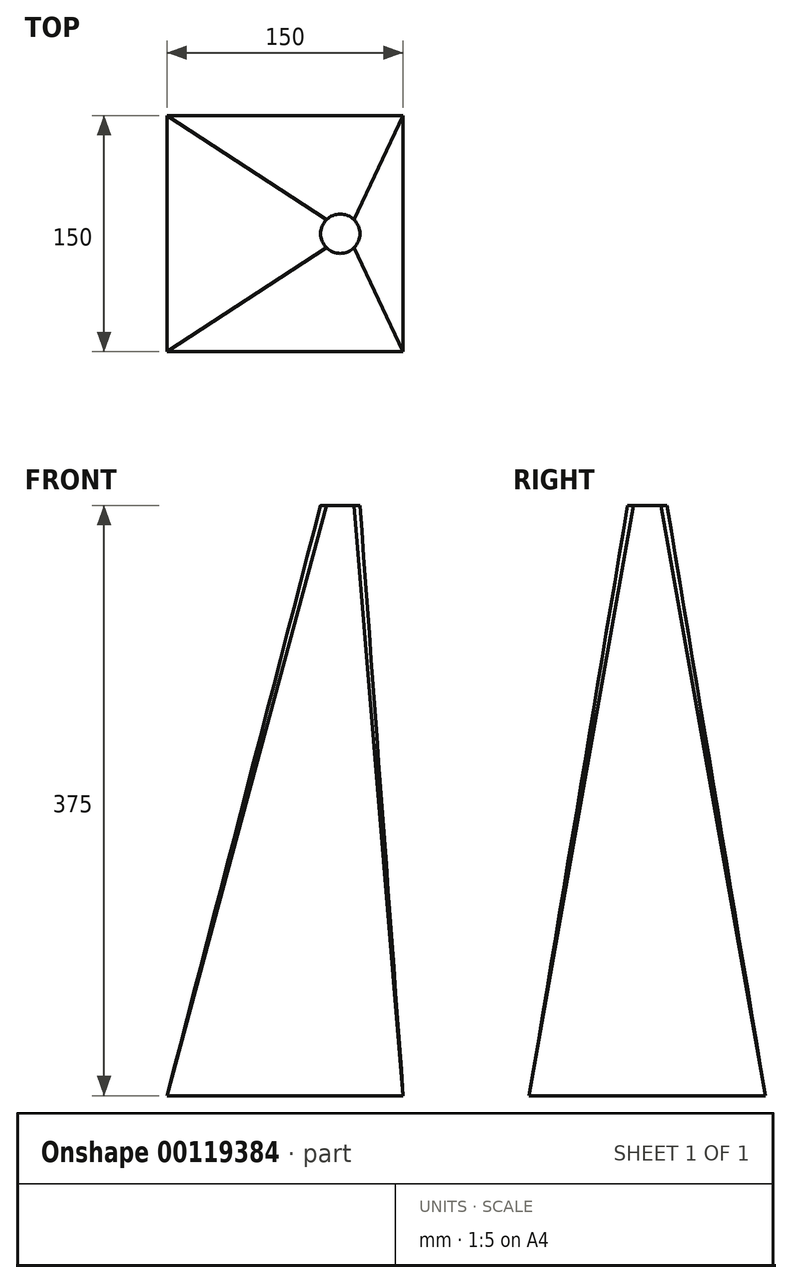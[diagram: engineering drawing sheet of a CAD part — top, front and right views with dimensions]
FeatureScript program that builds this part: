
annotation { "Feature Type Name" : "Feature", "Feature Type Description" : "" }
export const myFeature = defineFeature(function(context is Context, id is Id, definition is map)
    precondition{}
    {
        {
            var Q0;
            Q0=qCreatedBy(makeId("Top.planeOp"),FACE);
            var sketch = newSketch(context, id + "F0", { "sketchPlane" : qUnion([Q0])});
            skLineSegment(sketch, "E0.bottom", {"start": v(75, -75) * mm, "end": v(-75, -75) * mm});
            skLineSegment(sketch, "E0.top", {"start": v(75, 75) * mm, "end": v(-75, 75) * mm});
            skLineSegment(sketch, "E0.left", {"start": v(75, -75) * mm, "end": v(75, 75) * mm});
            skLineSegment(sketch, "E0.right", {"start": v(-75, -75) * mm, "end": v(-75, 75) * mm});
            skPoint(sketch, "E0.middle", {"position": v(0, 0) * mm});
            skSolve(sketch);
        }
        {
            var Q0;
            Q0=makeQuery(id+"F0.imprint","IMPRINT",FACE,{"disambiguationData":[TD([[makeQuery(id+"F0.imprint","IMPRINT",EDGE,{"derivedFrom":sQuery(id+"F0.wireOp",EDGE,"E0.bottom")}),-1.0]])]});
            cPlane(context, id + "F1", {"entities" : qUnion([Q0]), "cplaneType" : CPlaneType.OFFSET, "offset" : 375 * mm, "width" : 150 * mm, "height" : 150 * mm});
        }
        {
            var Q0;
            Q0=qCreatedBy(id+"F1.planeOp",FACE);
            var sketch = newSketch(context, id + "F2", { "sketchPlane" : qUnion([Q0])});
            skPoint(sketch, "E1.middle", {"position": v(35, 0) * mm});
            skLineSegment(sketch, "E2", {"start": v(35, 0) * mm, "end": v(26.16, -8.84) * mm, "construction": true});
            skLineSegment(sketch, "E3", {"start": v(35, 0) * mm, "end": v(26.16, 8.84) * mm, "construction": true});
            skLineSegment(sketch, "E4", {"start": v(35, 0) * mm, "end": v(43.84, 8.84) * mm, "construction": true});
            skLineSegment(sketch, "E5", {"start": v(35, 0) * mm, "end": v(43.84, -8.84) * mm, "construction": true});
            skArc(sketch, "E6", {"start": v(26.16, -8.84) * mm, "mid": v(35, -12.5) * mm, "end": v(43.84, -8.84) * mm});
            skArc(sketch, "E7", {"start": v(43.84, -8.84) * mm, "mid": v(47.5, 0) * mm, "end": v(43.84, 8.84) * mm});
            skLineSegment(sketch, "E8", {"start": v(43.84, 8.84) * mm, "end": v(43.84, 8.84) * mm});
            skArc(sketch, "E9", {"start": v(26.16, 8.84) * mm, "mid": v(22.5, 0) * mm, "end": v(26.16, -8.84) * mm});
            skArc(sketch, "E10", {"start": v(43.84, 8.84) * mm, "mid": v(35, 12.5) * mm, "end": v(26.16, 8.84) * mm});
            skSolve(sketch);
        }
        {
            var Q0;
            Q0=makeQuery(id+"F0.imprint","IMPRINT",FACE,{"disambiguationData":[TD([[makeQuery(id+"F0.imprint","IMPRINT",EDGE,{"derivedFrom":sQuery(id+"F0.wireOp",EDGE,"E0.bottom")}),-1.0]])]});
            var Q1;
            Q1=makeQuery(id+"F2.imprint","IMPRINT",FACE,{"disambiguationData":[TD([[makeQuery(id+"F2.imprint","IMPRINT",EDGE,{"derivedFrom":sQuery(id+"F2.wireOp",EDGE,"E6")}),1.0]])]});
            loft(context, id + "F3", {"sheetProfilesArray" : [{ "sheetProfileEntities" : qUnion([Q0]) }, { "sheetProfileEntities" : qUnion([Q1]) }]});
        }
    });
